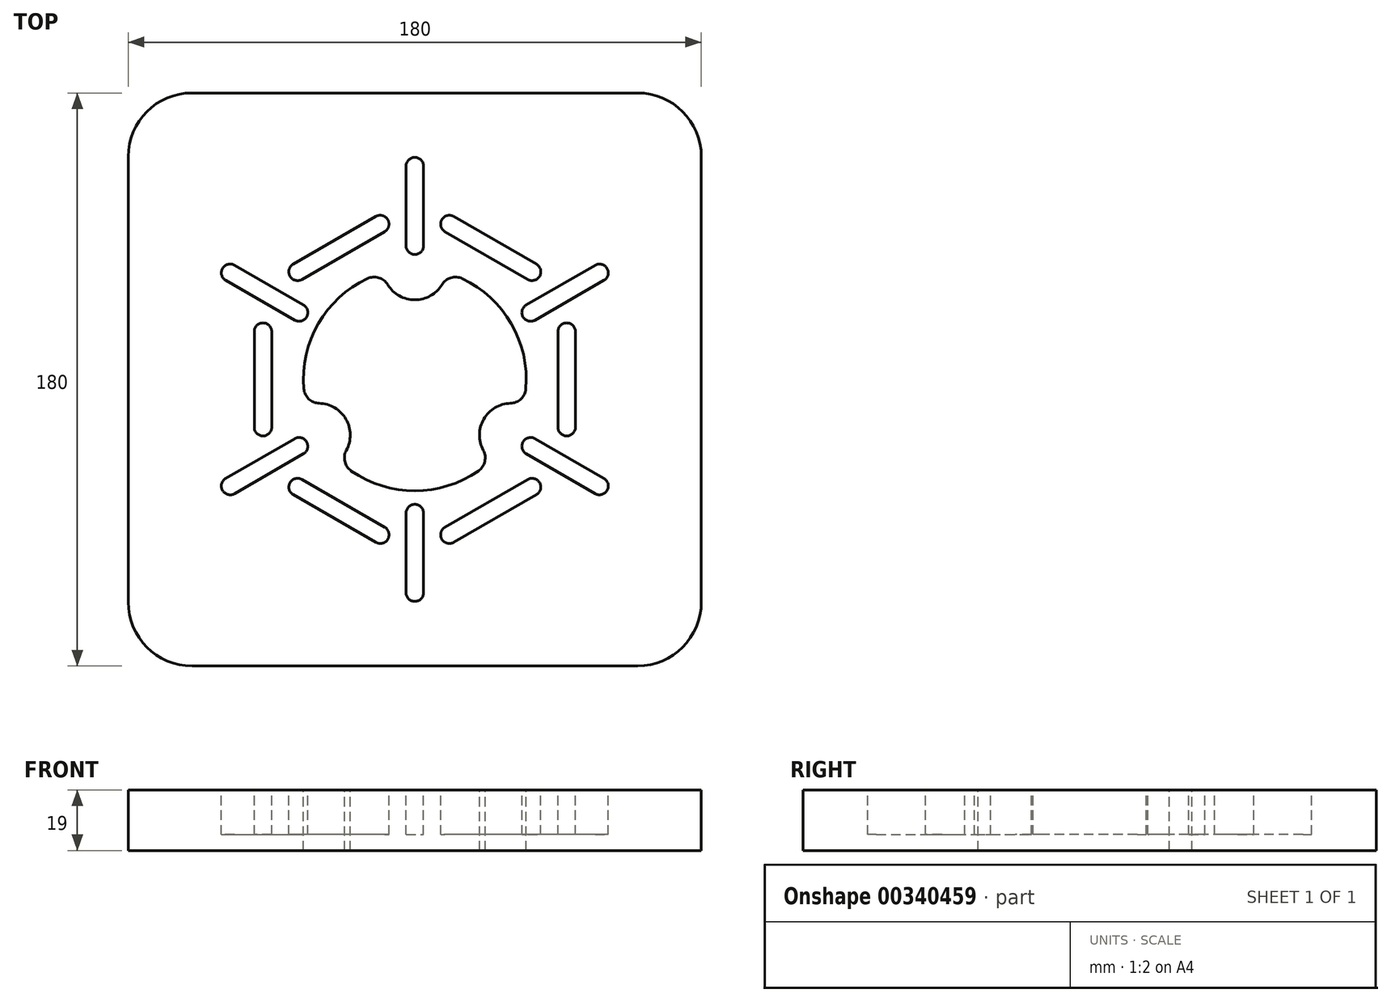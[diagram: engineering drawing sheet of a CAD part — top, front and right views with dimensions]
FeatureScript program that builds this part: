
annotation { "Feature Type Name" : "Feature", "Feature Type Description" : "" }
export const myFeature = defineFeature(function(context is Context, id is Id, definition is map)
    precondition{}
    {
        {
            var Q0;
            Q0=qCreatedBy(makeId("Top.planeOp"),FACE);
            var sketch = newSketch(context, id + "F0", { "sketchPlane" : qUnion([Q0])});
            skLineSegment(sketch, "E0.bottom", {"start": v(20, 0) * mm, "end": v(160, 0) * mm});
            skLineSegment(sketch, "E0.top", {"start": v(20, 180) * mm, "end": v(160, 180) * mm});
            skLineSegment(sketch, "E0.left", {"start": v(0, 20) * mm, "end": v(0, 160) * mm});
            skLineSegment(sketch, "E0.right", {"start": v(180, 20) * mm, "end": v(180, 160) * mm});
            skPoint(sketch, "E1.visualSharp", {"position": v(0, 180) * mm});
            skArc(sketch, "E1.filletArc", {"start": v(20, 180) * mm, "mid": v(5.86, 174.14) * mm, "end": v(0, 160) * mm});
            skPoint(sketch, "E2.visualSharp", {"position": v(180, 180) * mm});
            skArc(sketch, "E2.filletArc", {"start": v(180, 160) * mm, "mid": v(174.14, 174.14) * mm, "end": v(160, 180) * mm});
            skPoint(sketch, "E3.visualSharp", {"position": v(180, 0) * mm});
            skArc(sketch, "E3.filletArc", {"start": v(160, 0) * mm, "mid": v(174.14, 5.86) * mm, "end": v(180, 20) * mm});
            skPoint(sketch, "E4.visualSharp", {"position": v(0, 0) * mm});
            skArc(sketch, "E4.filletArc", {"start": v(0, 20) * mm, "mid": v(5.86, 5.86) * mm, "end": v(20, 0) * mm});
            skSolve(sketch);
        }
        {
            var Q0;
            Q0 = qSketchRegion(id + "F0", true);
            extrude(context, id + "F1", {"entities" : qUnion([Q0]), "depth" : 19 * mm});
        }
        {
            var Q0;
            Q0=makeQuery(id+"F1.opExtrude","CAP_FACE",FACE,{"disambiguationData":[OSD([sQuery(id+"F0.wireOp",EDGE,"E0.bottom"),sQuery(id+"F0.wireOp",EDGE,"E0.top"),sQuery(id+"F0.wireOp",EDGE,"E0.left"),sQuery(id+"F0.wireOp",EDGE,"E0.right"),sQuery(id+"F0.wireOp",EDGE,"E1.filletArc"),sQuery(id+"F0.wireOp",EDGE,"E2.filletArc"),sQuery(id+"F0.wireOp",EDGE,"E3.filletArc"),sQuery(id+"F0.wireOp",EDGE,"E4.filletArc")])],"isStart":false});
            var sketch = newSketch(context, id + "F2", { "sketchPlane" : qUnion([Q0])});
            skCircle(sketch, "E5", {"center": v(90, 90) * mm, "radius": 90 * mm, "construction": true});
            skPoint(sketch, "E5.first.point", {"position": v(0, 90) * mm});
            skPoint(sketch, "E5.second.point", {"position": v(90, 180) * mm});
            skPoint(sketch, "E5.third.point", {"position": v(180, 90) * mm});
            skLineSegment(sketch, "E6", {"start": v(42.3, 105) * mm, "end": v(42.3, 75) * mm});
            skLineSegment(sketch, "E7.anchor1", {"start": v(90, 90) * mm, "end": v(42.3, 75) * mm, "construction": true});
            skArc(sketch, "E8.0.startCap", {"start": v(39.55, 105) * mm, "mid": v(42.3, 107.75) * mm, "end": v(45.05, 105) * mm});
            skArc(sketch, "E8.0.endCap", {"start": v(45.05, 75) * mm, "mid": v(42.3, 72.25) * mm, "end": v(39.55, 75) * mm});
            skLineSegment(sketch, "E8.0.left", {"start": v(45.05, 105) * mm, "end": v(45.05, 75) * mm});
            skLineSegment(sketch, "E8.0.right", {"start": v(39.55, 105) * mm, "end": v(39.55, 75) * mm});
            skArc(sketch, "E9.1.0", {"start": v(54.54, 121.43) * mm, "mid": v(50.78, 122.43) * mm, "end": v(51.79, 126.19) * mm});
            skLineSegment(sketch, "E9.1.1", {"start": v(77.77, 141.19) * mm, "end": v(51.79, 126.19) * mm});
            skLineSegment(sketch, "E9.1.2", {"start": v(79.14, 138.8) * mm, "end": v(53.16, 123.8) * mm});
            skLineSegment(sketch, "E9.1.3", {"start": v(80.52, 136.43) * mm, "end": v(54.54, 121.43) * mm});
            skArc(sketch, "E9.1.4", {"start": v(77.77, 141.19) * mm, "mid": v(81.52, 140.18) * mm, "end": v(80.52, 136.43) * mm});
            skArc(sketch, "E9.2.0", {"start": v(99.48, 136.43) * mm, "mid": v(98.48, 140.18) * mm, "end": v(102.23, 141.19) * mm});
            skLineSegment(sketch, "E9.2.1", {"start": v(128.21, 126.19) * mm, "end": v(102.23, 141.19) * mm});
            skLineSegment(sketch, "E9.2.2", {"start": v(126.84, 123.8) * mm, "end": v(100.86, 138.8) * mm});
            skLineSegment(sketch, "E9.2.3", {"start": v(125.46, 121.43) * mm, "end": v(99.48, 136.43) * mm});
            skArc(sketch, "E9.2.4", {"start": v(128.21, 126.19) * mm, "mid": v(129.22, 122.43) * mm, "end": v(125.46, 121.43) * mm});
            skArc(sketch, "E9.3.0", {"start": v(134.95, 105) * mm, "mid": v(137.7, 107.75) * mm, "end": v(140.45, 105) * mm});
            skLineSegment(sketch, "E9.3.1", {"start": v(140.45, 75) * mm, "end": v(140.45, 105) * mm});
            skLineSegment(sketch, "E9.3.2", {"start": v(137.7, 75) * mm, "end": v(137.7, 105) * mm});
            skLineSegment(sketch, "E9.3.3", {"start": v(134.95, 75) * mm, "end": v(134.95, 105) * mm});
            skArc(sketch, "E9.3.4", {"start": v(140.45, 75) * mm, "mid": v(137.7, 72.25) * mm, "end": v(134.95, 75) * mm});
            skArc(sketch, "E9.4.0", {"start": v(125.46, 58.57) * mm, "mid": v(129.22, 57.57) * mm, "end": v(128.21, 53.81) * mm});
            skLineSegment(sketch, "E9.4.1", {"start": v(102.23, 38.81) * mm, "end": v(128.21, 53.81) * mm});
            skLineSegment(sketch, "E9.4.2", {"start": v(100.86, 41.2) * mm, "end": v(126.84, 56.2) * mm});
            skLineSegment(sketch, "E9.4.3", {"start": v(99.48, 43.57) * mm, "end": v(125.46, 58.57) * mm});
            skArc(sketch, "E9.4.4", {"start": v(102.23, 38.81) * mm, "mid": v(98.48, 39.82) * mm, "end": v(99.48, 43.57) * mm});
            skArc(sketch, "E9.5.0", {"start": v(80.52, 43.57) * mm, "mid": v(81.52, 39.82) * mm, "end": v(77.77, 38.81) * mm});
            skLineSegment(sketch, "E9.5.1", {"start": v(51.79, 53.81) * mm, "end": v(77.77, 38.81) * mm});
            skLineSegment(sketch, "E9.5.2", {"start": v(53.16, 56.2) * mm, "end": v(79.14, 41.2) * mm});
            skLineSegment(sketch, "E9.5.3", {"start": v(54.54, 58.57) * mm, "end": v(80.52, 43.57) * mm});
            skArc(sketch, "E9.5.4", {"start": v(51.79, 53.81) * mm, "mid": v(50.78, 57.57) * mm, "end": v(54.54, 58.57) * mm});
            skLineSegment(sketch, "E9.anchor1", {"start": v(90, 90) * mm, "end": v(39.55, 75) * mm, "construction": true});
            skLineSegment(sketch, "E9.anchor2", {"start": v(90, 90) * mm, "end": v(77.77, 38.81) * mm, "construction": true});
            skSolve(sketch);
        }
        {
            var Q0;
            Q0=makeQuery(id+"F2.imprint","IMPRINT",FACE,{"disambiguationData":[TD([[makeQuery(id+"F2.imprint","IMPRINT",EDGE,{"derivedFrom":makeQuery(id+"F1.opExtrude","CAP_EDGE",EDGE,{"disambiguationData":[OSD([sQuery(id+"F0.wireOp",EDGE,"E0.bottom")])],"isStart":false})}),1.0]])]});
            var sketch = newSketch(context, id + "F3", { "sketchPlane" : qUnion([Q0])});
            skLineSegment(sketch, "E10", {"start": v(90, 23) * mm, "end": v(90, 48) * mm});
            skLineSegment(sketch, "E11", {"start": v(90, 90) * mm, "end": v(0, 90) * mm, "construction": true});
            skPoint(sketch, "E12.center", {"position": v(90, 90) * mm});
            skLineSegment(sketch, "E12.anchor1", {"start": v(90, 90) * mm, "end": v(90, 23) * mm, "construction": true});
            skArc(sketch, "E13.0.startCap", {"start": v(92.75, 23) * mm, "mid": v(90, 20.25) * mm, "end": v(87.25, 23) * mm});
            skArc(sketch, "E13.0.endCap", {"start": v(87.25, 48) * mm, "mid": v(90, 50.75) * mm, "end": v(92.75, 48) * mm});
            skLineSegment(sketch, "E13.0.left", {"start": v(87.25, 23) * mm, "end": v(87.25, 48) * mm});
            skLineSegment(sketch, "E13.0.right", {"start": v(92.75, 23) * mm, "end": v(92.75, 48) * mm});
            skLineSegment(sketch, "E14.1.0", {"start": v(31.98, 56.5) * mm, "end": v(53.63, 69) * mm});
            skLineSegment(sketch, "E14.1.1", {"start": v(33.35, 54.12) * mm, "end": v(55, 66.62) * mm});
            skLineSegment(sketch, "E14.1.2", {"start": v(30.6, 58.88) * mm, "end": v(52.25, 71.38) * mm});
            skArc(sketch, "E14.1.3", {"start": v(52.25, 71.38) * mm, "mid": v(56, 70.38) * mm, "end": v(55, 66.62) * mm});
            skArc(sketch, "E14.1.4", {"start": v(33.35, 54.12) * mm, "mid": v(29.6, 55.13) * mm, "end": v(30.6, 58.88) * mm});
            skLineSegment(sketch, "E14.2.0", {"start": v(31.98, 123.5) * mm, "end": v(53.63, 111) * mm});
            skLineSegment(sketch, "E14.2.1", {"start": v(30.6, 121.12) * mm, "end": v(52.25, 108.62) * mm});
            skLineSegment(sketch, "E14.2.2", {"start": v(33.35, 125.88) * mm, "end": v(55, 113.38) * mm});
            skArc(sketch, "E14.2.3", {"start": v(55, 113.38) * mm, "mid": v(56, 109.63) * mm, "end": v(52.25, 108.62) * mm});
            skArc(sketch, "E14.2.4", {"start": v(30.6, 121.12) * mm, "mid": v(29.6, 124.88) * mm, "end": v(33.35, 125.88) * mm});
            skLineSegment(sketch, "E14.3.0", {"start": v(90, 157) * mm, "end": v(90, 132) * mm});
            skLineSegment(sketch, "E14.3.1", {"start": v(87.25, 157) * mm, "end": v(87.25, 132) * mm});
            skLineSegment(sketch, "E14.3.2", {"start": v(92.75, 157) * mm, "end": v(92.75, 132) * mm});
            skArc(sketch, "E14.3.3", {"start": v(92.75, 132) * mm, "mid": v(90, 129.25) * mm, "end": v(87.25, 132) * mm});
            skArc(sketch, "E14.3.4", {"start": v(87.25, 157) * mm, "mid": v(90, 159.75) * mm, "end": v(92.75, 157) * mm});
            skLineSegment(sketch, "E14.4.0", {"start": v(148.02, 123.5) * mm, "end": v(126.37, 111) * mm});
            skLineSegment(sketch, "E14.4.1", {"start": v(146.65, 125.88) * mm, "end": v(125, 113.38) * mm});
            skLineSegment(sketch, "E14.4.2", {"start": v(149.4, 121.12) * mm, "end": v(127.75, 108.62) * mm});
            skArc(sketch, "E14.4.3", {"start": v(127.75, 108.62) * mm, "mid": v(124, 109.63) * mm, "end": v(125, 113.38) * mm});
            skArc(sketch, "E14.4.4", {"start": v(146.65, 125.88) * mm, "mid": v(150.4, 124.88) * mm, "end": v(149.4, 121.12) * mm});
            skLineSegment(sketch, "E14.5.0", {"start": v(148.02, 56.5) * mm, "end": v(126.37, 69) * mm});
            skLineSegment(sketch, "E14.5.1", {"start": v(149.4, 58.88) * mm, "end": v(127.75, 71.38) * mm});
            skLineSegment(sketch, "E14.5.2", {"start": v(146.65, 54.12) * mm, "end": v(125, 66.62) * mm});
            skArc(sketch, "E14.5.3", {"start": v(125, 66.62) * mm, "mid": v(124, 70.38) * mm, "end": v(127.75, 71.38) * mm});
            skArc(sketch, "E14.5.4", {"start": v(149.4, 58.88) * mm, "mid": v(150.4, 55.13) * mm, "end": v(146.65, 54.12) * mm});
            skLineSegment(sketch, "E14.anchor1", {"start": v(90, 90) * mm, "end": v(87.25, 23) * mm, "construction": true});
            skLineSegment(sketch, "E14.anchor2", {"start": v(90, 90) * mm, "end": v(146.65, 54.12) * mm, "construction": true});
            skSolve(sketch);
        }
        {
            var Q0;
            Q0=makeQuery(id+"F2.imprint","IMPRINT",FACE,{"disambiguationData":[TD([[makeQuery(id+"F2.imprint","IMPRINT",EDGE,{"derivedFrom":makeQuery(id+"F1.opExtrude","CAP_EDGE",EDGE,{"disambiguationData":[OSD([sQuery(id+"F0.wireOp",EDGE,"E0.bottom")])],"isStart":false})}),1.0]])]});
            var sketch = newSketch(context, id + "F4", { "sketchPlane" : qUnion([Q0])});
            skArc(sketch, "E15", {"start": v(99.9, 123.57) * mm, "mid": v(120.31, 107.5) * mm, "end": v(124.02, 81.79) * mm});
            skArc(sketch, "E16", {"start": v(111.65, 77.5) * mm, "mid": v(117.04, 81.95) * mm, "end": v(124.02, 81.79) * mm});
            skArc(sketch, "E17", {"start": v(90, 115) * mm, "mid": v(96.55, 117.44) * mm, "end": v(99.9, 123.57) * mm});
            skArc(sketch, "E18.1.0", {"start": v(55.98, 81.79) * mm, "mid": v(59.69, 107.5) * mm, "end": v(80.1, 123.57) * mm});
            skArc(sketch, "E18.1.1", {"start": v(68.35, 77.5) * mm, "mid": v(62.96, 81.95) * mm, "end": v(55.98, 81.79) * mm});
            skArc(sketch, "E18.1.2", {"start": v(90, 115) * mm, "mid": v(83.45, 117.44) * mm, "end": v(80.1, 123.57) * mm});
            skArc(sketch, "E18.2.0", {"start": v(114.12, 64.64) * mm, "mid": v(90, 55) * mm, "end": v(65.88, 64.64) * mm});
            skArc(sketch, "E18.2.1", {"start": v(111.65, 77.5) * mm, "mid": v(110.5, 70.61) * mm, "end": v(114.12, 64.64) * mm});
            skArc(sketch, "E18.2.2", {"start": v(68.35, 77.5) * mm, "mid": v(69.5, 70.61) * mm, "end": v(65.88, 64.64) * mm});
            skSolve(sketch);
        }
        {
            var Q0;
            Q0 = qSketchRegion(id + "F4", true);
            extrude(context, id + "F5", {"entities" : qUnion([Q0]), "operationType" : NewBodyOperationType.REMOVE, "endBound" : BoundingType.THROUGH_ALL, "oppositeDirection" : true, "depth" : 25 * mm});
        }
        {
            var Q0;
            Q0 = qSketchRegion(id + "F2", true);
            var Q1;
            Q1 = qSketchRegion(id + "F3", true);
            extrude(context, id + "F6", {"entities" : qUnion([Q0, Q1]), "operationType" : NewBodyOperationType.REMOVE, "oppositeDirection" : true, "depth" : 14 * mm});
        }
        {
            var Q0;
            Q0=makeQuery(id+"F5.boolean.opBoolean","COPY",EDGE,{"derivedFrom":makeQuery(id+"F5.opExtrude","SWEPT_EDGE",EDGE,{"disambiguationData":[OSD([sQuery(id+"F4.wireOp",EDGE,"E18.1.0"),sQuery(id+"F4.wireOp",EDGE,"E18.1.2")])]})});
            var Q1;
            Q1=makeQuery(id+"F5.boolean.opBoolean","COPY",EDGE,{"derivedFrom":makeQuery(id+"F5.opExtrude","SWEPT_EDGE",EDGE,{"disambiguationData":[OSD([sQuery(id+"F4.wireOp",EDGE,"E15"),sQuery(id+"F4.wireOp",EDGE,"E17")])]})});
            var Q2;
            Q2=makeQuery(id+"F5.boolean.opBoolean","COPY",EDGE,{"derivedFrom":makeQuery(id+"F5.opExtrude","SWEPT_EDGE",EDGE,{"disambiguationData":[OSD([sQuery(id+"F4.wireOp",EDGE,"E18.1.0"),sQuery(id+"F4.wireOp",EDGE,"E18.1.1")])]})});
            var Q3;
            Q3=makeQuery(id+"F5.boolean.opBoolean","COPY",EDGE,{"derivedFrom":makeQuery(id+"F5.opExtrude","SWEPT_EDGE",EDGE,{"disambiguationData":[OSD([sQuery(id+"F4.wireOp",EDGE,"E18.2.0"),sQuery(id+"F4.wireOp",EDGE,"E18.2.2")])]})});
            var Q4;
            Q4=makeQuery(id+"F5.boolean.opBoolean","COPY",EDGE,{"derivedFrom":makeQuery(id+"F5.opExtrude","SWEPT_EDGE",EDGE,{"disambiguationData":[OSD([sQuery(id+"F4.wireOp",EDGE,"E18.2.0"),sQuery(id+"F4.wireOp",EDGE,"E18.2.1")])]})});
            var Q5;
            Q5=makeQuery(id+"F5.boolean.opBoolean","COPY",EDGE,{"derivedFrom":makeQuery(id+"F5.opExtrude","SWEPT_EDGE",EDGE,{"disambiguationData":[OSD([sQuery(id+"F4.wireOp",EDGE,"E15"),sQuery(id+"F4.wireOp",EDGE,"E16")])]})});
            fillet(context, id + "F7", {"entities" : qUnion([Q0, Q1, Q2, Q3, Q4, Q5]), "radius" : 5 * mm, "tangentPropagation" : true, "allowEdgeOverflow" : false});
        }
    });
